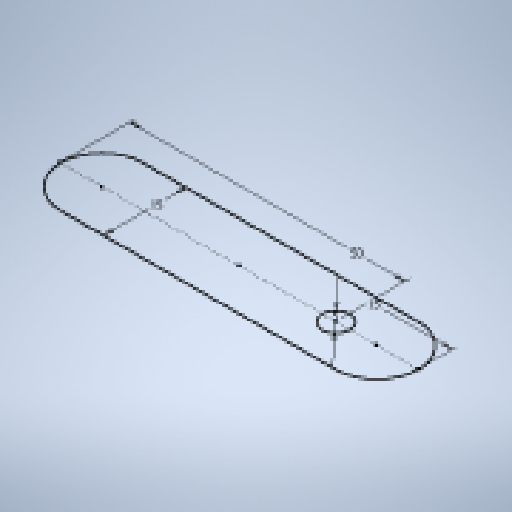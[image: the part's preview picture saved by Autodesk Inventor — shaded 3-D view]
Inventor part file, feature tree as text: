
AUTODESK INVENTOR PART (.ipt)
format: ipt  version: 2023 (Build 270158000, 158)  size: 250,368 bytes
history: native  units: mm
features: extrude x6, sketch x5, projected_geometry x4, other x2, mirror x2
ambient origin geometry x8: Origin, YZ Plane, XZ Plane, XY Plane, X Axis, Y Axis, Z Axis, Center Point
bodies: Body1 (feature_tree), Body2 (feature_tree)
feature tree (19):
  other  "實體1"
  extrude  "擠出1"  Depth=5.0mm
  extrude  "擠出2"  Depth=15.0mm
  extrude  "擠出3"  Depth=60.0mm
  extrude  "擠出4"  Depth=15.0mm
  sketch  "草圖5"
  extrude  "擠出5"  Depth=3.0mm TaperAngle=0.0deg
  extrude  "擠出6"  Depth=36.0mm
  mirror  "鏡射1"
  mirror  "鏡射2"
  sketch  "草圖1"
  sketch  "草圖2"
  projected_geometry  "投影迴路1"
  sketch  "草圖3"
  projected_geometry  "投影迴路2"
  sketch  "草圖4"
  projected_geometry  "投影迴路3"
  projected_geometry  "投影迴路4"
  other  "實體2"
